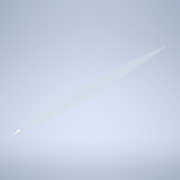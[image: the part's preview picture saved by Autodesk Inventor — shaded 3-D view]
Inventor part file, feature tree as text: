
AUTODESK INVENTOR PART (.ipt)
format: ipt  version: 2020 (Build 240168000, 168)  size: 450,048 bytes
history: native  units: mm
features: sketch x9, plane x4, projected_geometry x4, other x2, extrude x2, loft x2, surface_op x2
ambient origin geometry x8: Origin, YZ Plane, XZ Plane, XY Plane, X Axis, Y Axis, Z Axis, Center Point
bodies: Solid1 (feature_tree), Solid2 (feature_tree)
feature tree (25):
  sketch  "Sketch1"  dims[d0=10.0mm d1=105.0mm]
  plane  "Work Plane1"
  sketch  "Sketch2"  dims[d2=5.0mm d3=34.0mm]
  plane  "Work Plane2"
  sketch  "Sketch4"  dims[d4=200.0mm d5=-60.0mm]
  other  "Work Axis2"
  extrude  "Extrusion1"  Depth=10.0mm
  plane  "Work Plane3"
  plane  "Work Plane4"
  loft  "Loft2"
  extrude  "Extrusion2"  [1 undecoded]
  surface_op  "Replace Face1"
  loft  "Loft3"
  sketch  "Sketch11"  dims[d33=54.0mm d34=140.0mm d35=0.0mm d36=0.0mm]
  other  "Srf1"
  sketch  "Sketch12"  dims[d47=2.0mm]
  sketch  "Sketch13"  dims[d50=3.0mm d52=200.0mm d53=2.744546mm]
  sketch  "Sketch14"  dims[d54=-10.0mm d55=10.0mm d56=120.0mm d57=5.0mm d59=200.0mm d60=2.744546mm d61=0.0mm d62=90.0deg d63=0.0mm d64=90.0deg d65=0.0mm d66=90.0deg d67=0.0mm d68=90.0deg d70=0.0mm d71=90.0deg d76=7.5mm d77=0.0mm d78=0.0mm d79=5.0mm d80=2.0mm d81=5.0mm d82=3.0mm d83=0.0mm d84=8800.0mm d85=8800.0mm d86=8800.0mm d87=0.0mm d88=90.0deg d89=0.0mm d90=90.0deg d91=0.0mm d92=90.0deg]
  sketch  "Sketch8"  dims[d6=10.0mm d7=155.0mm d8=5.0mm d10=200.0mm d11=2.744546mm d12=-135.0mm]
  surface_op  "Boundary Patch1"
  sketch  "Sketch9"  dims[d19=5.0mm d20=5.0mm d22=200.0mm d23=2.744546mm]
  projected_geometry  "Project Cut Edges1"
  projected_geometry  "Project Cut Edges2"
  projected_geometry  "Project Cut Edges3"
  projected_geometry  "Project Cut Edges4"
note: 1 required parameter value undecoded (feature->parameter linkage not recoverable at this tier; creation-order binding heuristic only, values carry confidence <= 0.55)
